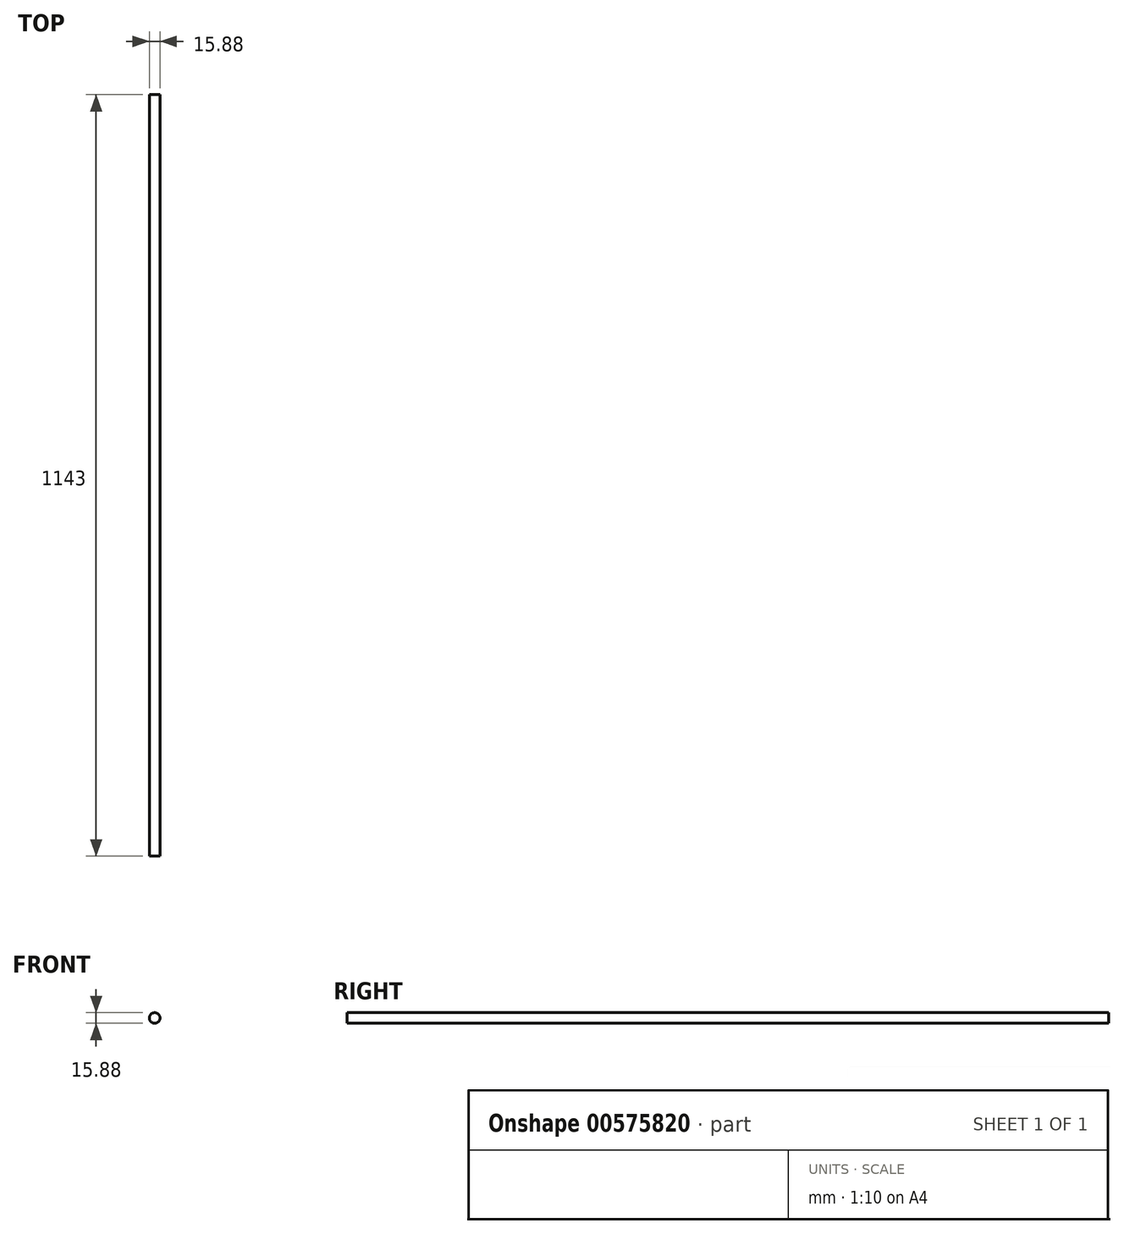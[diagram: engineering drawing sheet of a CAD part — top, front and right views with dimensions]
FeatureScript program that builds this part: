
annotation { "Feature Type Name" : "Feature", "Feature Type Description" : "" }
export const myFeature = defineFeature(function(context is Context, id is Id, definition is map)
    precondition{}
    {
        {
            var Q0;
            Q0=qCreatedBy(makeId("Front.planeOp"),FACE);
            var sketch = newSketch(context, id + "F0", { "sketchPlane" : qUnion([Q0])});
            skCircle(sketch, "E0", {"center": v(0, 0) * mm, "radius": 7.94 * mm});
            skSolve(sketch);
        }
        {
            var Q0;
            Q0 = qSketchRegion(id + "F0", true);
            extrude(context, id + "F1", {"entities" : qUnion([Q0]), "depth" : 1143 * mm, "offsetDistance" : 25.4 * mm});
        }
    });
